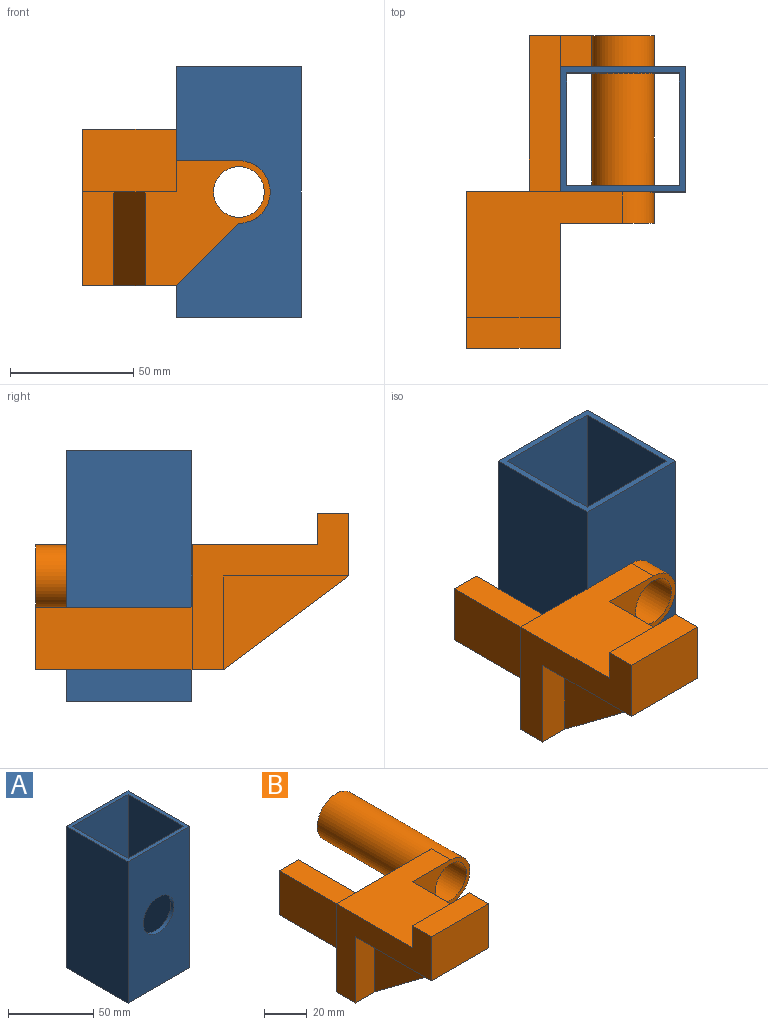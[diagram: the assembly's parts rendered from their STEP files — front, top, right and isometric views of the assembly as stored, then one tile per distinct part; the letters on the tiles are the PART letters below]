
ASSEMBLY  parts=2 mates=1
PART A: 12 faces, bbox 50.8x50.8x101.6 mm
  f0: plane 101.6x50.8mm, normal (0,1,0), area 4654.6mm2, adj f1,f7,f8,f9,f11
  f1: plane 101.6x50.8mm, normal (-1,0,0), area 5161.3mm2, adj f0,f2,f8,f9
  f2: plane 101.6x50.8mm, normal (0,-1,0), area 4654.6mm2, adj f1,f7,f8,f9,f10
  f3: plane 101.6x45.72mm, normal (1,0,0), area 4645.2mm2, adj f4,f6,f8,f9
  f4: plane 101.6x45.72mm, normal (0,-1,0), area 4138.4mm2, adj f3,f5,f8,f9,f11
  f5: plane 101.6x45.72mm, normal (-1,0,0), area 4645.2mm2, adj f4,f6,f8,f9
  f6: plane 101.6x45.72mm, normal (0,1,0), area 4138.4mm2, adj f3,f5,f8,f9,f10
  f7: plane 101.6x50.8mm, normal (1,0,0), area 5161.3mm2, adj f0,f2,f8,f9
  f8: plane 50.8x50.8mm, normal (0,0,1), area 490.3mm2, adj f0,f1,f2,f3,f4,f5,f6,f7
  f9: plane 50.8x50.8mm, normal (0,0,-1), area 490.3mm2, adj f0,f1,f2,f3,f4,f5,f6,f7
  f10: cylinder r=12.7mm len=25.4mm, axis (0,-1,0), area 202.7mm2, adj f2,f6
  f11: cylinder r=12.7mm len=25.4mm, axis (0,-1,0), area 202.7mm2, adj f0,f4
PART B: 26 faces, bbox 76.2x127x63.5 mm
  f0: plane 63.5x50.8mm, normal (0,1,0), area 2327.3mm2, adj f8,f9,f13,f15,f19,f21,f22,f25
  f1: plane 50.8x38.1mm, normal (0,-0.6,-0.8), area 806.4mm2, adj f2,f3,f12,f15
  f2: plane 50.8x38.1mm, normal (1,0,0), area 967.7mm2, adj f1,f4,f5
  f3: plane 50.8x38.1mm, normal (-1,0,0), area 967.7mm2, adj f1,f6,f20
  f4: plane 50.8x12.7mm, normal (0,0,-1), area 645.2mm2, adj f2,f5,f7,f12
  f5: plane 50.8x50.8mm, normal (0,-1,0), area 1372.5mm2, adj f2,f4,f7,f8,f15,f21,f22,f23
  f6: plane 50.8x12.7mm, normal (0,0,-1), area 645.2mm2, adj f3,f9,f12,f20
  f7: plane 50.8x25.4mm, normal (1,0,0), area 806.5mm2, adj f4,f5,f8,f10,f11,f12
  f8: plane 63.5x50.8mm, normal (0,0,1), area 2258.1mm2, adj f0,f5,f7,f9,f10,f22
  f9: plane 63.5x63.5mm, normal (-1,0,0), area 1451.6mm2, adj f0,f6,f8,f10,f11,f12,f15,f20
  f10: plane 38.1x12.7mm, normal (0,1,0), area 483.9mm2, adj f7,f8,f9,f11
  f11: plane 38.1x12.7mm, normal (0,0,1), area 483.9mm2, adj f7,f9,f10,f12
  f12: plane 38.1x25.4mm, normal (0,-1,0), area 967.7mm2, adj f1,f4,f6,f7,f9,f11
  f13: plane 63.5x12.7mm, normal (0,0,1), area 806.5mm2, adj f0,f16,f19,f25
  f14: plane 12.7x12.7mm, normal (0,-1,0), area 161.3mm2, adj f15,f17,f18,f19
  f15: plane 76.2x50.8mm, normal (0,0,-1), area 1451.6mm2, adj f0,f1,f5,f9,f14,f16,f18,f19
  f16: plane 25.4x25.4mm, normal (0,1,0), area 483.9mm2, adj f13,f15,f17,f18,f19,f25
  f17: plane 12.7x12.7mm, normal (0,0,1), area 161.3mm2, adj f14,f16,f18,f19
  f18: plane 12.7x12.7mm, normal (1,0,0), area 161.3mm2, adj f14,f15,f16,f17
  f19: plane 63.5x25.4mm, normal (1,0,0), area 1451.6mm2, adj f0,f13,f14,f15,f16,f17
  f20: plane 38.1x12.7mm, normal (0,-1,0), area 483.9mm2, adj f3,f6,f9,f15
  f21: plane 25.4x25.4mm, normal (0.71,0,-0.71), area 456.2mm2, adj f0,f5,f15,f22
  f22: cylinder r=12.7mm len=76.2mm, axis (0,-1,0), area 5573.8mm2, adj f0,f5,f8,f21,f24
  f23: cylinder r=10.29mm len=76.2mm, axis (0,-1,0), area 4925.2mm2, adj f5,f24
  f24: plane 25.4x25.4mm, normal (0,1,0), area 174.3mm2, adj f22,f23
  f25: plane 63.5x25.4mm, normal (-1,0,0), area 1612.9mm2, adj f0,f13,f15,f16
PLACE A at identity fixed
PLACE B rot(axis=(0,-1,0.01),0deg) t=(0,0,0)mm
MATE cylindrical B.f22 <-> A.f10  axis (0,-1,0) through (0,0,50.8)mm
